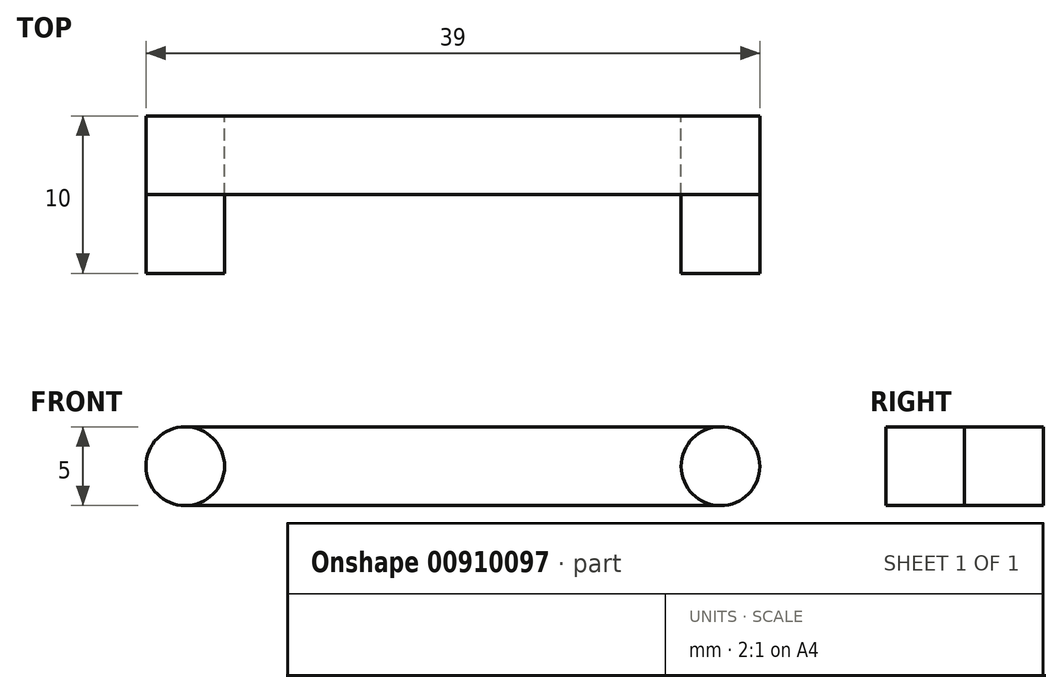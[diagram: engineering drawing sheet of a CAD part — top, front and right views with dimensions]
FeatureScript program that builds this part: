
annotation { "Feature Type Name" : "Feature", "Feature Type Description" : "" }
export const myFeature = defineFeature(function(context is Context, id is Id, definition is map)
    precondition{}
    {
        {
            var Q0;
            Q0=qCreatedBy(makeId("Front.planeOp"),FACE);
            var sketch = newSketch(context, id + "F0", { "sketchPlane" : qUnion([Q0])});
            skCircle(sketch, "E0", {"center": v(0, 0) * mm, "radius": 2.5 * mm});
            skCircle(sketch, "E1", {"center": v(34, 0) * mm, "radius": 2.5 * mm});
            skLineSegment(sketch, "E2.bottom", {"start": v(0, 2.5) * mm, "end": v(34, 2.5) * mm});
            skLineSegment(sketch, "E2.top", {"start": v(0, -2.5) * mm, "end": v(34, -2.5) * mm});
            skLineSegment(sketch, "E2.left", {"start": v(0, 2.5) * mm, "end": v(0, -2.5) * mm});
            skLineSegment(sketch, "E2.right", {"start": v(34, 2.5) * mm, "end": v(34, -2.5) * mm});
            skSolve(sketch);
        }
        {
            var Q0;
            Q0=makeQuery(id+"F0.imprint","IMPRINT",FACE,{"disambiguationData":[TD([[makeQuery(id+"F0.imprint","IMPRINT",EDGE,{"derivedFrom":sQuery(id+"F0.wireOp",EDGE,"E0")}),1.0]])]});
            var Q1;
            Q1=makeQuery(id+"F0.imprint","IMPRINT",FACE,{"disambiguationData":[TD([[makeQuery(id+"F0.imprint","IMPRINT",EDGE,{"derivedFrom":sQuery(id+"F0.wireOp",EDGE,"E1")}),1.0]])]});
            extrude(context, id + "F1", {"entities" : qUnion([Q0, Q1]), "depth" : 10 * mm, "offsetDistance" : 25 * mm});
        }
        {
            var Q0;
            Q0 = qSketchRegion(id + "F0", true);
            extrude(context, id + "F2", {"entities" : qUnion([Q0]), "depth" : 5 * mm, "offsetDistance" : 25 * mm});
        }
    });
